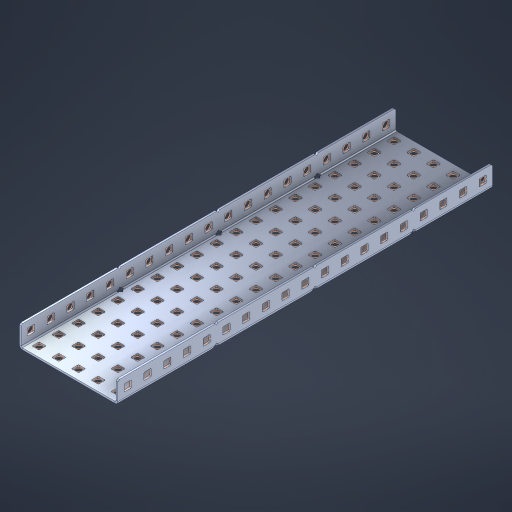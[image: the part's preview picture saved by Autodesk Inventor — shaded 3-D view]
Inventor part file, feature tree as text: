
AUTODESK INVENTOR PART (.ipt)
format: ipt  version: 2023 (Build 270158000, 158)  size: 1,606,144 bytes
history: native  units: in
note: dims shown in document units (in); Inventor stores cm internally (conversion verified against a paired STEP export)
features: other x138, extrude x132, sheet_metal_op x10, sketch x8, mirror x1, pattern_linear x1, chamfer x1
ambient origin geometry x8: Origin, YZ Plane, XZ Plane, XY Plane, X Axis, Y Axis, Z Axis, Center Point
bodies: Solid1 (feature_tree), Body (feature_tree)
feature tree (291):
  other  "Flange Pattern Plane"
  sheet_metal_op  "Flange Pattern"
  sheet_metal_op  "Body Pattern"
  other  "Arc Length"
  mirror  "Notch Mirror"
  pattern_linear  "Notch Pattern"  Spacing1=0.1875in  [1 undecoded]
  chamfer  "End Chamfer"
  extrude  "Half Cut"  Depth=0.0469in
  sketch  "Sketch1"  dims[d0=2.5in]
  other  "Plate1"
  sketch  "Sketch2"  dims[d1=9.5in]
  other  "Plate2"
  sheet_metal_op  "Bend1"
  sheet_metal_op  "Corner1"
  sketch  "Sketch3"  dims[d2=0.0469in]
  other  "Flange Pattern Sketch"
  sketch  "Sketch7"  dims[d3=0.0469in]
  other  "Srf1"
  other  "Srf2"
  sketch  "Sketch8"  dims[d4=0.0234in]
  sketch  "Sketch9"  dims[d5=0.0938in]
  other  "Srf91"
  sheet_metal_op  "Body Pattern Sketch"
  other  "Srf92"
  sketch  "Sketch13"  dims[d6=0.0469in]
  sketch  "Sketch14"  dims[d7=0.5in d8=90.0deg d9=0.0312in d10=0.1875in d11=0.0469in d12=0.0469in d16=0.182in d17=0.02in d18=0.0469in d19=0.0in d20=0.25in d21=0.25in d46=0.172in d47=1.0in d48=0.0in d49=0.182in d50=0.02in d51=0.25in d52=0.25in d53=0.0469in d54=0.0in d55=0.172in d56=1.0in d57=0.0in d60=7.4803in d62=0.5in d63=1.9685in d65=0.5in d85=0.1227in d86=0.1659in d88=0.04in d89=0.0469in d90=0.0in d91=0.04in d92=0.0491in d95=2.5in d96=0.04in d97=0.25in d98=45.0deg d101=0.0in d102=2.497in d131=2.5in d132=7.4803in d134=0.5in d139=0.5in]
  other  "Srf856"
  other  "Srf1310"
  other  "Srf1311"
  other  "Srf1312"
  other  "Srf1376"
  other  "Srf1377"
  other  "Srf1728"
  other  "Srf1755"
  other  "Srf1878"
  other  "Srf1879"
  other  "Srf1880"
  other  "Srf1881"
  other  "Srf1882"
  other  "Srf1883"
  other  "Srf1884"
  other  "Srf1885"
  other  "Srf1886"
  other  "Srf1887"
  other  "Srf1888"
  other  "Srf1889"
  other  "Srf1890"
  other  "Srf1891"
  other  "Srf1892"
  other  "Srf1893"
  other  "Srf1894"
  other  "Srf1895"
  other  "Srf1896"
  other  "Srf1897"
  other  "Srf1898"
  other  "Srf1899"
  other  "Srf1900"
  other  "Srf1901"
  other  "Srf1902"
  other  "Srf1903"
  other  "Srf1904"
  other  "Srf1905"
  other  "Srf1906"
  other  "Srf1942"
  other  "Srf1943"
  other  "Srf1944"
  other  "Srf1945"
  other  "Srf1946"
  other  "Srf1947"
  other  "Srf1948"
  other  "Srf1949"
  other  "Srf1950"
  other  "Srf1951"
  other  "Srf1952"
  other  "Srf1953"
  other  "Srf1954"
  other  "Srf1955"
  other  "Srf1956"
  other  "Srf1957"
  other  "Srf1958"
  other  "Srf1959"
  other  "Srf1960"
  other  "Srf1961"
  other  "Srf1962"
  other  "Srf1963"
  other  "Srf1964"
  other  "Srf1965"
  other  "Srf1966"
  other  "Srf1967"
  other  "Srf1968"
  other  "Srf1969"
  other  "Srf1970"
  other  "Srf2111"
  other  "Srf2112"
  other  "Srf2113"
  other  "Srf2146"
  other  "Srf2147"
  other  "Srf2148"
  other  "Srf2149"
  other  "Srf2150"
  other  "Srf2151"
  other  "Srf2152"
  other  "Srf2153"
  other  "Srf2154"
  other  "Srf2155"
  other  "Srf2156"
  other  "Srf2157"
  other  "Srf2158"
  other  "Srf2159"
  other  "Srf2160"
  other  "Srf2161"
  other  "Srf2162"
  other  "Srf2163"
  other  "Srf2164"
  other  "Srf2165"
  other  "Srf2166"
  other  "Srf2167"
  other  "Srf2168"
  other  "Srf2169"
  other  "Srf2170"
  other  "Srf2171"
  other  "Srf2172"
  other  "Srf2173"
  other  "Srf2174"
  other  "Srf2175"
  other  "Srf2176"
  other  "Srf2177"
  other  "Srf2178"
  other  "Srf2179"
  other  "Srf2180"
  other  "Srf2181"
  other  "Srf2182"
  other  "Srf2183"
  other  "Srf2184"
  other  "Srf2185"
  other  "Srf2186"
  other  "Srf2187"
  other  "Srf2188"
  other  "Srf2189"
  other  "Srf2190"
  other  "Srf2191"
  other  "Srf2192"
  other  "Srf2193"
  other  "Srf2194"
  other  "Srf2195"
  other  "Srf2196"
  other  "Srf2197"
  other  "Srf2198"
  other  "Srf2199"
  other  "Srf2200"
  other  "Srf2201"
  other  "Srf2202"
  other  "Srf2203"
  other  "Srf2204"
  other  "Srf2205"
  sheet_metal_op  "Flange Stamp"
  sheet_metal_op  "Flange Circle"
  sheet_metal_op  "Body Stamp"
  sheet_metal_op  "Body Circle"
  sheet_metal_op  "Notch"
  extrude  "ExtrusionSrf2"  Depth=0.0469in
  extrude  "ExtrusionSrf92"  Depth=2.5in
  extrude  "ExtrusionSrf856"  Depth=0.02in
  extrude  "ExtrusionSrf1310"  Depth=0.0469in
  extrude  "ExtrusionSrf1311"  TaperAngle=0.0deg  [1 undecoded]
  extrude  "ExtrusionSrf1312"  Depth=0.25in
  extrude  "ExtrusionSrf1376"  Depth=0.25in
  extrude  "ExtrusionSrf1377"  Depth=2.5in
  extrude  "ExtrusionSrf1728"  Depth=2.5in TaperAngle=0.0deg
  extrude  "ExtrusionSrf1755"  Depth=2.5in
  extrude  "ExtrusionSrf1878"  Depth=0.02in
  extrude  "ExtrusionSrf1879"  Depth=0.25in
  extrude  "ExtrusionSrf1880"  Depth=0.25in
  extrude  "ExtrusionSrf1881"  Depth=0.0469in
  extrude  "ExtrusionSrf1882"  TaperAngle=0.0deg  [1 undecoded]
  extrude  "ExtrusionSrf1883"  Depth=2.5in
  extrude  "ExtrusionSrf1884"  Depth=2.5in TaperAngle=0.0deg
  extrude  "ExtrusionSrf1885"  Depth=2.5in
  extrude  "ExtrusionSrf1886"  Depth=2.5in
  extrude  "ExtrusionSrf1887"  Depth=2.5in
  extrude  "ExtrusionSrf1888"  Depth=2.5in
  extrude  "ExtrusionSrf1889"  Depth=2.5in
  extrude  "ExtrusionSrf1890"  Depth=0.0469in
  extrude  "ExtrusionSrf1891"  TaperAngle=0.0deg  [1 undecoded]
  extrude  "ExtrusionSrf1892"  Depth=2.5in
  extrude  "ExtrusionSrf1893"  Depth=2.5in
  extrude  "ExtrusionSrf1894"  Depth=2.5in
  extrude  "ExtrusionSrf1895"  Depth=0.25in TaperAngle=45.0deg
  extrude  "ExtrusionSrf1896"  TaperAngle=0.0deg  [1 undecoded]
  extrude  "ExtrusionSrf1897"  Depth=2.5in
  extrude  "ExtrusionSrf1898"  Depth=2.5in
  extrude  "ExtrusionSrf1899"  Depth=2.5in
  extrude  "ExtrusionSrf1900"  Depth=2.5in
  extrude  "ExtrusionSrf1901"  Depth=2.5in
  extrude  "ExtrusionSrf1902"  [1 undecoded]
  extrude  "ExtrusionSrf1903"  [1 undecoded]
  extrude  "ExtrusionSrf1904"  [1 undecoded]
  extrude  "ExtrusionSrf1905"  [1 undecoded]
  extrude  "ExtrusionSrf1906"  [1 undecoded]
  extrude  "ExtrusionSrf1942"  [1 undecoded]
  extrude  "ExtrusionSrf1943"  [1 undecoded]
  extrude  "ExtrusionSrf1944"  [1 undecoded]
  extrude  "ExtrusionSrf1945"  [1 undecoded]
  extrude  "ExtrusionSrf1946"  [1 undecoded]
  extrude  "ExtrusionSrf1947"  [1 undecoded]
  extrude  "ExtrusionSrf1948"  [1 undecoded]
  extrude  "ExtrusionSrf1949"  [1 undecoded]
  extrude  "ExtrusionSrf1950"  [1 undecoded]
  extrude  "ExtrusionSrf1951"  [1 undecoded]
  extrude  "ExtrusionSrf1952"  [1 undecoded]
  extrude  "ExtrusionSrf1953"  [1 undecoded]
  extrude  "ExtrusionSrf1954"  [1 undecoded]
  extrude  "ExtrusionSrf1955"  [1 undecoded]
  extrude  "ExtrusionSrf1956"  [1 undecoded]
  extrude  "ExtrusionSrf1957"  [1 undecoded]
  extrude  "ExtrusionSrf1958"  [1 undecoded]
  extrude  "ExtrusionSrf1959"  [1 undecoded]
  extrude  "ExtrusionSrf1960"  [1 undecoded]
  extrude  "ExtrusionSrf1961"  [1 undecoded]
  extrude  "ExtrusionSrf1962"  [1 undecoded]
  extrude  "ExtrusionSrf1963"  [1 undecoded]
  extrude  "ExtrusionSrf1964"  [1 undecoded]
  extrude  "ExtrusionSrf1965"  [1 undecoded]
  extrude  "ExtrusionSrf1966"  [1 undecoded]
  extrude  "ExtrusionSrf1967"  [1 undecoded]
  extrude  "ExtrusionSrf1968"  [1 undecoded]
  extrude  "ExtrusionSrf1969"  [1 undecoded]
  extrude  "ExtrusionSrf1970"  [1 undecoded]
  extrude  "ExtrusionSrf2111"  [1 undecoded]
  extrude  "ExtrusionSrf2112"  [1 undecoded]
  extrude  "ExtrusionSrf2113"  [1 undecoded]
  extrude  "ExtrusionSrf2146"  [1 undecoded]
  extrude  "ExtrusionSrf2147"  [1 undecoded]
  extrude  "ExtrusionSrf2148"  [1 undecoded]
  extrude  "ExtrusionSrf2149"  [1 undecoded]
  extrude  "ExtrusionSrf2150"  [1 undecoded]
  extrude  "ExtrusionSrf2151"  [1 undecoded]
  extrude  "ExtrusionSrf2152"  [1 undecoded]
  extrude  "ExtrusionSrf2153"  [1 undecoded]
  extrude  "ExtrusionSrf2154"  [1 undecoded]
  extrude  "ExtrusionSrf2155"  [1 undecoded]
  extrude  "ExtrusionSrf2156"  [1 undecoded]
  extrude  "ExtrusionSrf2157"  [1 undecoded]
  extrude  "ExtrusionSrf2158"  [1 undecoded]
  extrude  "ExtrusionSrf2159"  [1 undecoded]
  extrude  "ExtrusionSrf2160"  [1 undecoded]
  extrude  "ExtrusionSrf2161"  [1 undecoded]
  extrude  "ExtrusionSrf2162"  [1 undecoded]
  extrude  "ExtrusionSrf2163"  [1 undecoded]
  extrude  "ExtrusionSrf2164"  [1 undecoded]
  extrude  "ExtrusionSrf2165"  [1 undecoded]
  extrude  "ExtrusionSrf2166"  [1 undecoded]
  extrude  "ExtrusionSrf2167"  [1 undecoded]
  extrude  "ExtrusionSrf2168"  [1 undecoded]
  extrude  "ExtrusionSrf2169"  [1 undecoded]
  extrude  "ExtrusionSrf2170"  [1 undecoded]
  extrude  "ExtrusionSrf2171"  [1 undecoded]
  extrude  "ExtrusionSrf2172"  [1 undecoded]
  extrude  "ExtrusionSrf2173"  [1 undecoded]
  extrude  "ExtrusionSrf2174"  [1 undecoded]
  extrude  "ExtrusionSrf2175"  [1 undecoded]
  extrude  "ExtrusionSrf2176"  [1 undecoded]
  extrude  "ExtrusionSrf2177"  [1 undecoded]
  extrude  "ExtrusionSrf2178"  [1 undecoded]
  extrude  "ExtrusionSrf2179"  [1 undecoded]
  extrude  "ExtrusionSrf2180"  [1 undecoded]
  extrude  "ExtrusionSrf2181"  [1 undecoded]
  extrude  "ExtrusionSrf2182"  [1 undecoded]
  extrude  "ExtrusionSrf2183"  [1 undecoded]
  extrude  "ExtrusionSrf2184"  [1 undecoded]
  extrude  "ExtrusionSrf2185"  [1 undecoded]
  extrude  "ExtrusionSrf2186"  [1 undecoded]
  extrude  "ExtrusionSrf2187"  [1 undecoded]
  extrude  "ExtrusionSrf2188"  [1 undecoded]
  extrude  "ExtrusionSrf2189"  [1 undecoded]
  extrude  "ExtrusionSrf2190"  [1 undecoded]
  extrude  "ExtrusionSrf2191"  [1 undecoded]
  extrude  "ExtrusionSrf2192"  [1 undecoded]
  extrude  "ExtrusionSrf2193"  [1 undecoded]
  extrude  "ExtrusionSrf2194"  [1 undecoded]
  extrude  "ExtrusionSrf2195"  [1 undecoded]
  extrude  "ExtrusionSrf2196"  [1 undecoded]
  extrude  "ExtrusionSrf2197"  [1 undecoded]
  extrude  "ExtrusionSrf2198"  [1 undecoded]
  extrude  "ExtrusionSrf2199"  [1 undecoded]
  extrude  "ExtrusionSrf2200"  [1 undecoded]
  extrude  "ExtrusionSrf2201"  [1 undecoded]
  extrude  "ExtrusionSrf2202"  [1 undecoded]
  extrude  "ExtrusionSrf2203"  [1 undecoded]
  extrude  "ExtrusionSrf2204"  [1 undecoded]
  extrude  "ExtrusionSrf2205"  [1 undecoded]
note: 102 required parameter values undecoded (feature->parameter linkage not recoverable at this tier; creation-order binding heuristic only, values carry confidence <= 0.55)
